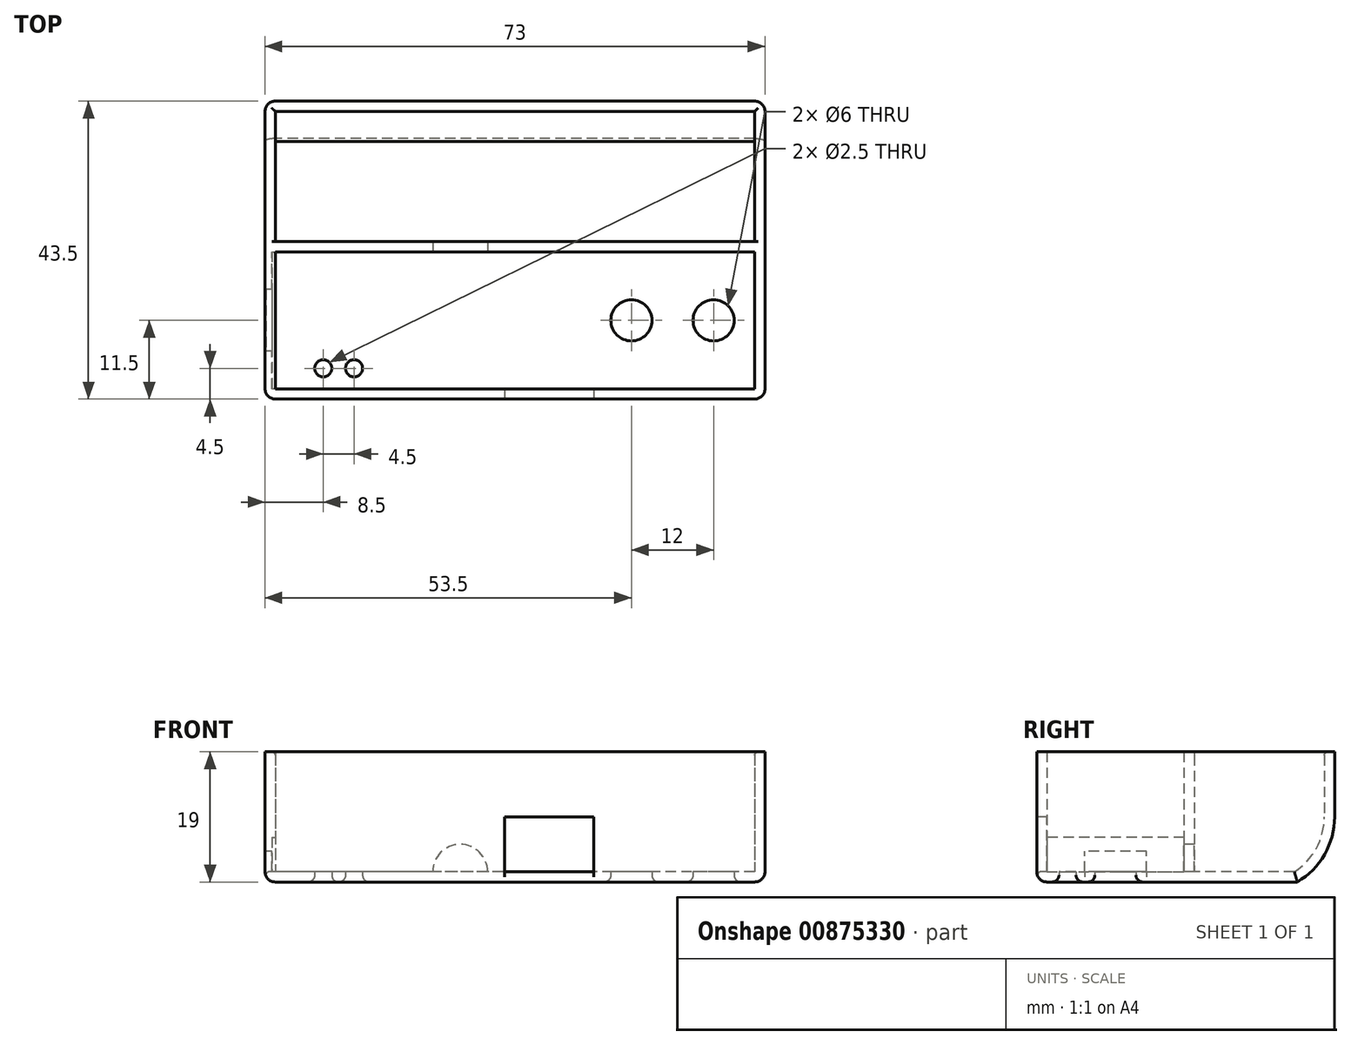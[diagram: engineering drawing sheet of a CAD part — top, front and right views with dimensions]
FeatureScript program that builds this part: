
annotation { "Feature Type Name" : "Feature", "Feature Type Description" : "" }
export const myFeature = defineFeature(function(context is Context, id is Id, definition is map)
    precondition{}
    {
        {
            var Q0;
            Q0=qCreatedBy(makeId("Top.planeOp"),FACE);
            var sketch = newSketch(context, id + "F0", { "sketchPlane" : qUnion([Q0])});
            skLineSegment(sketch, "E0.bottom", {"start": v(0, 0) * mm, "end": v(70, 0) * mm});
            skLineSegment(sketch, "E0.top", {"start": v(0, 19) * mm, "end": v(70, 19) * mm});
            skLineSegment(sketch, "E0.left", {"start": v(0, 0) * mm, "end": v(0, 19) * mm});
            skLineSegment(sketch, "E0.right", {"start": v(70, 0) * mm, "end": v(70, 19) * mm});
            skLineSegment(sketch, "E1.bottom", {"start": v(-1.5, 20.5) * mm, "end": v(71.5, 20.5) * mm});
            skLineSegment(sketch, "E1.top", {"start": v(-1.5, -1.5) * mm, "end": v(71.5, -1.5) * mm});
            skLineSegment(sketch, "E1.left", {"start": v(-1.5, 20.5) * mm, "end": v(-1.5, -1.5) * mm});
            skLineSegment(sketch, "E1.right", {"start": v(71.5, 20.5) * mm, "end": v(71.5, -1.5) * mm});
            skLineSegment(sketch, "E2.bottom", {"start": v(0, -1.5) * mm, "end": v(70, -1.5) * mm});
            skLineSegment(sketch, "E2.top", {"start": v(0, -21.5) * mm, "end": v(70, -21.5) * mm});
            skLineSegment(sketch, "E2.left", {"start": v(0, -1.5) * mm, "end": v(0, -21.5) * mm});
            skLineSegment(sketch, "E2.right", {"start": v(70, -1.5) * mm, "end": v(70, -21.5) * mm});
            skLineSegment(sketch, "E3.top", {"start": v(-1.5, -23) * mm, "end": v(71.5, -23) * mm});
            skLineSegment(sketch, "E3.left", {"start": v(-1.5, -1.5) * mm, "end": v(-1.5, -23) * mm});
            skLineSegment(sketch, "E3.right", {"start": v(71.5, -1.5) * mm, "end": v(71.5, -23) * mm});
            skCircle(sketch, "E4", {"center": v(64, -11.5) * mm, "radius": 3 * mm});
            skCircle(sketch, "E5", {"center": v(52, -11.5) * mm, "radius": 3 * mm});
            skLineSegment(sketch, "E6.bottom", {"start": v(70, -5) * mm, "end": v(46.5, -5) * mm, "construction": true});
            skLineSegment(sketch, "E6.top", {"start": v(70, -18) * mm, "end": v(46.5, -18) * mm, "construction": true});
            skLineSegment(sketch, "E6.left", {"start": v(70, -5) * mm, "end": v(70, -18) * mm, "construction": true});
            skLineSegment(sketch, "E6.right", {"start": v(46.5, -5) * mm, "end": v(46.5, -18) * mm, "construction": true});
            skLineSegment(sketch, "E7.top", {"start": v(46.5, -6) * mm, "end": v(33.5, -6) * mm, "construction": true});
            skLineSegment(sketch, "E7.right", {"start": v(33.5, -23) * mm, "end": v(33.5, -6) * mm, "construction": true});
            skLineSegment(sketch, "E8", {"start": v(33.5, -23) * mm, "end": v(46.5, -23) * mm});
            skLineSegment(sketch, "E9", {"start": v(46.5, -23) * mm, "end": v(46.5, -6) * mm, "construction": true});
            skLineSegment(sketch, "E10.bottom", {"start": v(0, -4) * mm, "end": v(33.5, -4) * mm, "construction": true});
            skLineSegment(sketch, "E10.top", {"start": v(0, -19) * mm, "end": v(33.5, -19) * mm, "construction": true});
            skLineSegment(sketch, "E10.left", {"start": v(0, -4) * mm, "end": v(0, -19) * mm, "construction": true});
            skLineSegment(sketch, "E10.right", {"start": v(33.5, -4) * mm, "end": v(33.5, -19) * mm, "construction": true});
            skLineSegment(sketch, "E11.bottom", {"start": v(0, -3) * mm, "end": v(27, -3) * mm, "construction": true});
            skLineSegment(sketch, "E11.top", {"start": v(0, -20) * mm, "end": v(27, -20) * mm, "construction": true});
            skLineSegment(sketch, "E11.left", {"start": v(0, -3) * mm, "end": v(0, -20) * mm, "construction": true});
            skLineSegment(sketch, "E11.right", {"start": v(27, -3) * mm, "end": v(27, -20) * mm, "construction": true});
            skLineSegment(sketch, "E12", {"start": v(40, -23) * mm, "end": v(40, -6) * mm, "construction": true});
            skLineSegment(sketch, "E13", {"start": v(0, -11.5) * mm, "end": v(27, -11.5) * mm, "construction": true});
            skCircle(sketch, "E14", {"center": v(7, -18.5) * mm, "radius": 1.25 * mm});
            skCircle(sketch, "E15", {"center": v(11.5, -18.5) * mm, "radius": 1.25 * mm});
            skSolve(sketch);
        }
        {
            var Q0;
            Q0=makeQuery(id+"F0.imprint","IMPRINT",FACE,{"disambiguationData":[TD([[makeQuery(id+"F0.imprint","IMPRINT",EDGE,{"derivedFrom":sQuery(id+"F0.wireOp",EDGE,"E0.bottom")}),1.0]])]});
            var Q1;
            Q1=makeQuery(id+"F0.imprint","IMPRINT",FACE,{"disambiguationData":[TD([[makeQuery(id+"F0.imprint","IMPRINT",EDGE,{"derivedFrom":sQuery(id+"F0.wireOp",EDGE,"E0.bottom")}),-1.0]])]});
            var Q2;
            Q2=makeQuery(id+"F0.imprint","IMPRINT",FACE,{"disambiguationData":[TD([[makeQuery(id+"F0.imprint","IMPRINT",EDGE,{"derivedFrom":sQuery(id+"F0.wireOp",EDGE,"E2.top")}),-1.0]])]});
            var Q3;
            Q3=makeQuery(id+"F0.imprint","IMPRINT",FACE,{"disambiguationData":[TD([[makeQuery(id+"F0.imprint","IMPRINT",EDGE,{"derivedFrom":sQuery(id+"F0.wireOp",EDGE,"E2.top")}),1.0]])]});
            extrude(context, id + "F1", {"entities" : qUnion([Q0, Q1, Q2, Q3]), "depth" : 1.5 * mm, "offsetDistance" : 25 * mm});
        }
        {
            var Q0;
            Q0=makeQuery(id+"F0.imprint","IMPRINT",FACE,{"disambiguationData":[TD([[makeQuery(id+"F0.imprint","IMPRINT",EDGE,{"derivedFrom":sQuery(id+"F0.wireOp",EDGE,"E0.bottom")}),-1.0]])]});
            var Q1;
            Q1=makeQuery(id+"F0.imprint","IMPRINT",FACE,{"disambiguationData":[TD([[makeQuery(id+"F0.imprint","IMPRINT",EDGE,{"derivedFrom":sQuery(id+"F0.wireOp",EDGE,"E2.top")}),-1.0]])]});
            extrude(context, id + "F2", {"entities" : qUnion([Q0, Q1]), "operationType" : NewBodyOperationType.ADD, "depth" : 19 * mm, "offsetDistance" : 25 * mm});
        }
        {
            var Q0;
            {var subQ0=sQuery(id+"F0.wireOp",EDGE,"E3.left");var subQ1=sQuery(id+"F0.wireOp",EDGE,"E1.left");Q0=makeQuery(id+"F2.boolean.opBoolean","MERGE",FACE,{"derivedFrom":[makeQuery(id+"F1.opExtrude","SWEPT_FACE",FACE,{"disambiguationData":[OSD([subQ1,subQ0])]}),makeQuery(id+"F2.opExtrude","SWEPT_FACE",FACE,{"disambiguationData":[OSD([subQ1,subQ0])]})]});}
            var sketch = newSketch(context, id + "F3", { "sketchPlane" : qUnion([Q0])});
            skCircle(sketch, "E16", {"center": v(-9.5, 9.5) * mm, "radius": 9.5 * mm});
            skCircle(sketch, "E17", {"center": v(-9.5, 9.5) * mm, "radius": 11 * mm});
            skLineSegment(sketch, "E18", {"start": v(-19, 19) * mm, "end": v(-19, 0) * mm, "construction": true});
            skLineSegment(sketch, "E19", {"start": v(-19, 3.95) * mm, "end": v(-19, 9.5) * mm});
            skSolve(sketch);
        }
        {
            var Q0;
            {var subQ0=sQuery(id+"F3.wireOp",EDGE,"E17");var subQ1=sQuery(id+"F0.wireOp",EDGE,"E1.left");var subQ5=makeQuery(id+"F1.opExtrude","CAP_EDGE",EDGE,{"disambiguationData":[OSD([subQ1,sQuery(id+"F0.wireOp",EDGE,"E3.left")])],"isStart":true});var subQ6=makeQuery(id+"F3.imprint","INTERSECT",VERTEX,{"disambiguationData":[OD(0.0)],"derivedFrom":[subQ5,subQ0]});Q0=makeQuery(id+"F3.imprint","IMPRINT",FACE,{"disambiguationData":[TD([[makeQuery(id+"F3.imprint","IMPRINT",EDGE,{"disambiguationData":[TD([[subQ6,1.0]])],"derivedFrom":subQ0}),-1.0]])]});}
            extrude(context, id + "F4", {"entities" : qUnion([Q0]), "operationType" : NewBodyOperationType.REMOVE, "endBound" : BoundingType.UP_TO_NEXT, "oppositeDirection" : true, "depth" : 25 * mm, "offsetDistance" : 25 * mm});
        }
        {
            var Q0;
            {var subQ0=sQuery(id+"F3.wireOp",EDGE,"E19");Q0=makeQuery(id+"F3.imprint","IMPRINT",FACE,{"disambiguationData":[TD([[makeQuery(id+"F3.imprint","IMPRINT",EDGE,{"derivedFrom":subQ0}),-1.0]])]});}
            extrude(context, id + "F5", {"entities" : qUnion([Q0]), "operationType" : NewBodyOperationType.ADD, "oppositeDirection" : true, "depth" : 72 * mm, "offsetDistance" : 25 * mm});
        }
        {
            var Q0;
            {var subQ0=sQuery(id+"F0.wireOp",EDGE,"E8");var subQ1=sQuery(id+"F0.wireOp",EDGE,"E3.top");Q0=makeQuery(id+"F2.boolean.opBoolean","MERGE",FACE,{"derivedFrom":[makeQuery(id+"F1.opExtrude","SWEPT_FACE",FACE,{"disambiguationData":[OSD([subQ1,subQ0])]}),makeQuery(id+"F2.opExtrude","SWEPT_FACE",FACE,{"disambiguationData":[OSD([subQ1,subQ0])]})]});}
            var sketch = newSketch(context, id + "F6", { "sketchPlane" : qUnion([Q0])});
            skLineSegment(sketch, "E20.bottom", {"start": v(33.5, 0) * mm, "end": v(46.5, 0) * mm});
            skLineSegment(sketch, "E20.top", {"start": v(33.5, 9.5) * mm, "end": v(46.5, 9.5) * mm});
            skLineSegment(sketch, "E20.left", {"start": v(33.5, 0) * mm, "end": v(33.5, 9.5) * mm});
            skLineSegment(sketch, "E20.right", {"start": v(46.5, 0) * mm, "end": v(46.5, 9.5) * mm});
            skLineSegment(sketch, "E21", {"start": v(46.5, 1.5) * mm, "end": v(33.5, 1.5) * mm});
            skSolve(sketch);
        }
        {
            var Q0;
            {var subQ0=sQuery(id+"F6.wireOp",EDGE,"E20.top");Q0=makeQuery(id+"F6.imprint","IMPRINT",FACE,{"disambiguationData":[TD([[makeQuery(id+"F6.imprint","IMPRINT",EDGE,{"derivedFrom":subQ0}),-1.0]])]});}
            extrude(context, id + "F7", {"entities" : qUnion([Q0]), "operationType" : NewBodyOperationType.REMOVE, "oppositeDirection" : true, "depth" : 1.5 * mm, "offsetDistance" : 25 * mm});
        }
        {
            var Q0;
            {var subQ0=sQuery(id+"F0.wireOp",EDGE,"E3.left");var subQ1=sQuery(id+"F0.wireOp",EDGE,"E1.left");Q0=makeQuery(id+"F2.boolean.opBoolean","MERGE",FACE,{"derivedFrom":[makeQuery(id+"F1.opExtrude","SWEPT_FACE",FACE,{"disambiguationData":[OSD([subQ1,subQ0])]}),makeQuery(id+"F2.opExtrude","SWEPT_FACE",FACE,{"disambiguationData":[OSD([subQ1,subQ0])]})]});}
            var sketch = newSketch(context, id + "F8", { "sketchPlane" : qUnion([Q0])});
            skLineSegment(sketch, "E22.bottom", {"start": v(7, 0) * mm, "end": v(16, 0) * mm});
            skLineSegment(sketch, "E22.top", {"start": v(7, 4.5) * mm, "end": v(16, 4.5) * mm});
            skLineSegment(sketch, "E22.left", {"start": v(7, 0) * mm, "end": v(7, 4.5) * mm});
            skLineSegment(sketch, "E22.right", {"start": v(16, 0) * mm, "end": v(16, 4.5) * mm});
            skLineSegment(sketch, "E23", {"start": v(7, 1.5) * mm, "end": v(16, 1.5) * mm});
            skSolve(sketch);
        }
        {
            var Q0;
            {var subQ0=sQuery(id+"F8.wireOp",EDGE,"E22.top");Q0=makeQuery(id+"F8.imprint","IMPRINT",FACE,{"disambiguationData":[TD([[makeQuery(id+"F8.imprint","IMPRINT",EDGE,{"derivedFrom":subQ0}),-1.0]])]});}
            extrude(context, id + "F9", {"entities" : qUnion([Q0]), "operationType" : NewBodyOperationType.REMOVE, "oppositeDirection" : true, "depth" : 1.5 * mm, "offsetDistance" : 25 * mm});
        }
        {
            var Q0;
            Q0=makeQuery(id+"F2.opExtrude","SWEPT_FACE",FACE,{"disambiguationData":[OSD([sQuery(id+"F0.wireOp",EDGE,"E2.left")])]});
            var sketch = newSketch(context, id + "F10", { "sketchPlane" : qUnion([Q0])});
            skLineSegment(sketch, "E24.bottom", {"start": v(-1.5, 1.5) * mm, "end": v(-21.5, 1.5) * mm});
            skLineSegment(sketch, "E24.top", {"start": v(-1.5, 6.5) * mm, "end": v(-21.5, 6.5) * mm});
            skLineSegment(sketch, "E24.left", {"start": v(-1.5, 1.5) * mm, "end": v(-1.5, 6.5) * mm});
            skLineSegment(sketch, "E24.right", {"start": v(-21.5, 1.5) * mm, "end": v(-21.5, 6.5) * mm});
            skSolve(sketch);
        }
        {
            var Q0;
            Q0=makeQuery(id+"F10.imprint","IMPRINT",FACE,{"disambiguationData":[TD([[makeQuery(id+"F10.imprint","IMPRINT",EDGE,{"derivedFrom":sQuery(id+"F10.wireOp",EDGE,"E24.top")}),1.0]])]});
            extrude(context, id + "F11", {"entities" : qUnion([Q0]), "operationType" : NewBodyOperationType.REMOVE, "oppositeDirection" : true, "depth" : 0.5 * mm, "offsetDistance" : 25 * mm});
        }
        {
            var Q0;
            Q0=makeQuery(id+"F11.boolean.opBoolean","MERGE",FACE,{"derivedFrom":[makeQuery(id+"F2.opExtrude","SWEPT_FACE",FACE,{"disambiguationData":[OSD([sQuery(id+"F0.wireOp",EDGE,"E1.top")])]})],"fromTools":[makeQuery(id+"F11.opExtrude","SWEPT_FACE",FACE,{"disambiguationData":[OSD([sQuery(id+"F10.wireOp",EDGE,"E24.left")])]})]});
            var sketch = newSketch(context, id + "F12", { "sketchPlane" : qUnion([Q0])});
            skCircle(sketch, "E25", {"center": v(27, 1.5) * mm, "radius": 4 * mm});
            skSolve(sketch);
        }
        {
            var Q0;
            {var subQ0=sQuery(id+"F12.wireOp",EDGE,"E25");var subQ1=makeQuery(id+"F11.boolean.opBoolean","MERGE",EDGE,{"derivedFrom":[makeQuery(id+"F2.boolean.opBoolean","INTERSECT",EDGE,{"derivedFrom":[makeQuery(id+"F1.opExtrude","CAP_FACE",FACE,{"disambiguationData":[OSD([sQuery(id+"F0.wireOp",EDGE,"E1.bottom"),sQuery(id+"F0.wireOp",EDGE,"E1.left"),sQuery(id+"F0.wireOp",EDGE,"E1.right"),sQuery(id+"F0.wireOp",EDGE,"E3.top"),sQuery(id+"F0.wireOp",EDGE,"E3.left"),sQuery(id+"F0.wireOp",EDGE,"E3.right"),sQuery(id+"F0.wireOp",EDGE,"E4"),sQuery(id+"F0.wireOp",EDGE,"E5"),sQuery(id+"F0.wireOp",EDGE,"E8"),sQuery(id+"F0.wireOp",EDGE,"E14"),sQuery(id+"F0.wireOp",EDGE,"E15")])],"isStart":false}),makeQuery(id+"F2.opExtrude","SWEPT_FACE",FACE,{"disambiguationData":[OSD([sQuery(id+"F0.wireOp",EDGE,"E1.top")])]})]})],"fromTools":[makeQuery(id+"F11.opExtrude","SWEPT_EDGE",EDGE,{"disambiguationData":[OSD([sQuery(id+"F10.wireOp",EDGE,"E24.bottom"),sQuery(id+"F10.wireOp",EDGE,"E24.left")])]})]});var subQ2=makeQuery(id+"F12.imprint","INTERSECT",VERTEX,{"disambiguationData":[OD(0.0)],"derivedFrom":[subQ1,subQ0]});Q0=makeQuery(id+"F12.imprint","IMPRINT",FACE,{"disambiguationData":[TD([[makeQuery(id+"F12.imprint","IMPRINT",EDGE,{"disambiguationData":[TD([[subQ2,-1.0]])],"derivedFrom":subQ0}),1.0]])]});}
            extrude(context, id + "F13", {"entities" : qUnion([Q0]), "operationType" : NewBodyOperationType.REMOVE, "oppositeDirection" : true, "depth" : 1.5 * mm, "offsetDistance" : 25 * mm});
        }
        {
            var Q0;
            {var subQ0=sQuery(id+"F0.wireOp",EDGE,"E3.left");var subQ1=sQuery(id+"F0.wireOp",EDGE,"E3.top");Q0=makeQuery(id+"F2.boolean.opBoolean","MERGE",EDGE,{"derivedFrom":[makeQuery(id+"F1.opExtrude","SWEPT_EDGE",EDGE,{"disambiguationData":[OSD([subQ1,subQ0])]}),makeQuery(id+"F2.opExtrude","SWEPT_EDGE",EDGE,{"disambiguationData":[OSD([subQ1,subQ0])]})]});}
            var Q1;
            Q1=makeQuery(id+"F1.opExtrude","CAP_EDGE",EDGE,{"disambiguationData":[OSD([sQuery(id+"F0.wireOp",EDGE,"E1.left"),sQuery(id+"F0.wireOp",EDGE,"E3.left")])],"isStart":true});
            var Q2;
            Q2=makeQuery(id+"F1.opExtrude","CAP_EDGE",EDGE,{"disambiguationData":[OSD([sQuery(id+"F0.wireOp",EDGE,"E3.top"),sQuery(id+"F0.wireOp",EDGE,"E8")])],"isStart":true});
            var Q3;
            {var subQ0=sQuery(id+"F0.wireOp",EDGE,"E3.right");var subQ1=sQuery(id+"F0.wireOp",EDGE,"E3.top");Q3=makeQuery(id+"F2.boolean.opBoolean","MERGE",EDGE,{"derivedFrom":[makeQuery(id+"F1.opExtrude","SWEPT_EDGE",EDGE,{"disambiguationData":[OSD([subQ1,subQ0])]}),makeQuery(id+"F2.opExtrude","SWEPT_EDGE",EDGE,{"disambiguationData":[OSD([subQ1,subQ0])]})]});}
            var Q4;
            {var subQ0=sQuery(id+"F0.wireOp",EDGE,"E1.right");var subQ1=sQuery(id+"F0.wireOp",EDGE,"E1.bottom");Q4=makeQuery(id+"F2.boolean.opBoolean","MERGE",EDGE,{"derivedFrom":[makeQuery(id+"F1.opExtrude","SWEPT_EDGE",EDGE,{"disambiguationData":[OSD([subQ1,subQ0])]}),makeQuery(id+"F2.opExtrude","SWEPT_EDGE",EDGE,{"disambiguationData":[OSD([subQ1,subQ0])]})]});}
            var Q5;
            Q5=makeQuery(id+"F4.boolean.opBoolean","COPY",EDGE,{"derivedFrom":makeQuery(id+"F4.opExtrude","CAP_EDGE",EDGE,{"disambiguationData":[OSD([sQuery(id+"F3.wireOp",EDGE,"E17")])],"isStart":false})});
            var Q6;
            Q6=makeQuery(id+"F1.opExtrude","CAP_EDGE",EDGE,{"disambiguationData":[OSD([sQuery(id+"F0.wireOp",EDGE,"E1.right"),sQuery(id+"F0.wireOp",EDGE,"E3.right")])],"isStart":true});
            var Q7;
            {var subQ0=sQuery(id+"F0.wireOp",EDGE,"E1.left");var subQ1=sQuery(id+"F0.wireOp",EDGE,"E1.bottom");Q7=makeQuery(id+"F2.boolean.opBoolean","MERGE",EDGE,{"derivedFrom":[makeQuery(id+"F1.opExtrude","SWEPT_EDGE",EDGE,{"disambiguationData":[OSD([subQ1,subQ0])]}),makeQuery(id+"F2.opExtrude","SWEPT_EDGE",EDGE,{"disambiguationData":[OSD([subQ1,subQ0])]})]});}
            var Q8;
            Q8=makeQuery(id+"F4.boolean.opBoolean","COPY",EDGE,{"derivedFrom":makeQuery(id+"F4.opExtrude","CAP_EDGE",EDGE,{"disambiguationData":[OSD([sQuery(id+"F3.wireOp",EDGE,"E17")])],"isStart":true})});
            fillet(context, id + "F14", {"entities" : qUnion([Q0, Q1, Q2, Q3, Q4, Q5, Q6, Q7, Q8]), "radius" : 1.5 * mm, "tangentPropagation" : true, "allowEdgeOverflow" : false});
        }
        {
            var Q0;
            Q0=makeQuery(id+"F1.opExtrude","CAP_EDGE",EDGE,{"disambiguationData":[OSD([sQuery(id+"F0.wireOp",EDGE,"E5")])],"isStart":true});
            var Q1;
            Q1=makeQuery(id+"F1.opExtrude","CAP_EDGE",EDGE,{"disambiguationData":[OSD([sQuery(id+"F0.wireOp",EDGE,"E4")])],"isStart":true});
            var Q2;
            Q2=makeQuery(id+"F1.opExtrude","CAP_EDGE",EDGE,{"disambiguationData":[OSD([sQuery(id+"F0.wireOp",EDGE,"E14")])],"isStart":true});
            var Q3;
            Q3=makeQuery(id+"F1.opExtrude","CAP_EDGE",EDGE,{"disambiguationData":[OSD([sQuery(id+"F0.wireOp",EDGE,"E15")])],"isStart":true});
            var Q4;
            Q4=makeQuery(id+"F9.boolean.opBoolean","COPY",EDGE,{"derivedFrom":makeQuery(id+"F9.opExtrude","CAP_EDGE",EDGE,{"disambiguationData":[OSD([sQuery(id+"F8.wireOp",EDGE,"E22.top")])],"isStart":true})});
            var Q5;
            Q5=makeQuery(id+"F9.boolean.opBoolean","COPY",EDGE,{"derivedFrom":makeQuery(id+"F9.opExtrude","CAP_EDGE",EDGE,{"disambiguationData":[OSD([sQuery(id+"F8.wireOp",EDGE,"E22.right")])],"isStart":true})});
            var Q6;
            Q6=makeQuery(id+"F9.boolean.opBoolean","COPY",EDGE,{"derivedFrom":makeQuery(id+"F9.opExtrude","CAP_EDGE",EDGE,{"disambiguationData":[OSD([sQuery(id+"F8.wireOp",EDGE,"E22.left")])],"isStart":true})});
            var Q7;
            Q7=makeQuery(id+"F7.boolean.opBoolean","COPY",EDGE,{"derivedFrom":makeQuery(id+"F7.opExtrude","CAP_EDGE",EDGE,{"disambiguationData":[OSD([sQuery(id+"F6.wireOp",EDGE,"E20.top")])],"isStart":true})});
            var Q8;
            Q8=makeQuery(id+"F7.boolean.opBoolean","COPY",EDGE,{"derivedFrom":makeQuery(id+"F7.opExtrude","CAP_EDGE",EDGE,{"disambiguationData":[OSD([sQuery(id+"F6.wireOp",EDGE,"E20.right")])],"isStart":true})});
            var Q9;
            Q9=makeQuery(id+"F7.boolean.opBoolean","COPY",EDGE,{"derivedFrom":makeQuery(id+"F7.opExtrude","CAP_EDGE",EDGE,{"disambiguationData":[OSD([sQuery(id+"F6.wireOp",EDGE,"E20.left")])],"isStart":true})});
            var Q10;
            Q10=makeQuery(id+"F13.boolean.opBoolean","COPY",EDGE,{"derivedFrom":makeQuery(id+"F13.opExtrude","CAP_EDGE",EDGE,{"disambiguationData":[OSD([sQuery(id+"F12.wireOp",EDGE,"E25")])],"isStart":true})});
            var Q11;
            Q11=makeQuery(id+"F13.boolean.opBoolean","COPY",EDGE,{"derivedFrom":makeQuery(id+"F13.opExtrude","CAP_EDGE",EDGE,{"disambiguationData":[OSD([sQuery(id+"F12.wireOp",EDGE,"E25")])],"isStart":false})});
            fillet(context, id + "F15", {"entities" : qUnion([Q0, Q1, Q2, Q3, Q4, Q5, Q6, Q7, Q8, Q9, Q10, Q11]), "radius" : 1 * mm, "tangentPropagation" : true, "allowEdgeOverflow" : false});
        }
        {
            var Q0;
            {var subQ0=sQuery(id+"F0.wireOp",EDGE,"E8");var subQ1=sQuery(id+"F0.wireOp",EDGE,"E3.top");var subQ2=makeQuery(id+"F2.boolean.opBoolean","MERGE",FACE,{"derivedFrom":[makeQuery(id+"F1.opExtrude","SWEPT_FACE",FACE,{"disambiguationData":[OSD([subQ1,subQ0])]}),makeQuery(id+"F2.opExtrude","SWEPT_FACE",FACE,{"disambiguationData":[OSD([subQ1,subQ0])]})]});var subQ3=makeQuery(id+"F1.opExtrude","CAP_EDGE",EDGE,{"disambiguationData":[OSD([subQ1,subQ0])],"isStart":true});var subQ4=sQuery(id+"F10.wireOp",EDGE,"E24.left");var subQ5=sQuery(id+"F10.wireOp",EDGE,"E24.bottom");var subQ6=sQuery(id+"F0.wireOp",EDGE,"E15");var subQ7=sQuery(id+"F0.wireOp",EDGE,"E14");var subQ8=sQuery(id+"F0.wireOp",EDGE,"E5");var subQ9=sQuery(id+"F0.wireOp",EDGE,"E4");var subQ10=sQuery(id+"F0.wireOp",EDGE,"E3.right");var subQ11=sQuery(id+"F0.wireOp",EDGE,"E3.left");var subQ12=sQuery(id+"F0.wireOp",EDGE,"E1.top");var subQ13=sQuery(id+"F0.wireOp",EDGE,"E1.right");var subQ14=sQuery(id+"F0.wireOp",EDGE,"E1.left");var subQ15=sQuery(id+"F0.wireOp",EDGE,"E1.bottom");var subQ16=makeQuery(id+"F1.opExtrude","CAP_FACE",FACE,{"disambiguationData":[OSD([subQ15,subQ14,subQ13,subQ1,subQ11,subQ10,subQ9,subQ8,subQ0,subQ7,subQ6])],"isStart":false});Q0=makeQuery(id+"F15.opFillet","MERGE",EDGE,{"derivedFrom":[makeQuery(id+"F14.opFillet","BLEND_EDGE",EDGE,{"blendedFrom":[subQ3,makeQuery(id+"F13.boolean.opBoolean","MERGE",FACE,{"derivedFrom":[makeQuery(id+"F2.boolean.opBoolean","SPLIT",FACE,{"disambiguationData":[TD([makeQuery(id+"F2.opExtrude","SWEPT_FACE",FACE,{"disambiguationData":[OSD([sQuery(id+"F0.wireOp",EDGE,"E0.bottom")])]})])],"derivedFrom":subQ16}),makeQuery(id+"F11.boolean.opBoolean","MERGE",FACE,{"derivedFrom":[makeQuery(id+"F9.boolean.opBoolean","MERGE",FACE,{"derivedFrom":[makeQuery(id+"F7.boolean.opBoolean","MERGE",FACE,{"derivedFrom":[makeQuery(id+"F2.boolean.opBoolean","SPLIT",FACE,{"disambiguationData":[TD([makeQuery(id+"F1.opExtrude","SWEPT_FACE",FACE,{"disambiguationData":[OSD([subQ9])]})])],"derivedFrom":subQ16})],"fromTools":[makeQuery(id+"F7.opExtrude","SWEPT_FACE",FACE,{"disambiguationData":[OSD([sQuery(id+"F6.wireOp",EDGE,"E21")])]})]})],"fromTools":[makeQuery(id+"F9.opExtrude","SWEPT_FACE",FACE,{"disambiguationData":[OSD([sQuery(id+"F8.wireOp",EDGE,"E23")])]})]})],"fromTools":[makeQuery(id+"F11.opExtrude","SWEPT_FACE",FACE,{"disambiguationData":[OSD([subQ5]),TDD([makeQuery(id+"F10.imprint","IMPRINT",EDGE,{"disambiguationData":[TD([[makeQuery(id+"F10.imprint","INTERSECT",VERTEX,{"derivedFrom":[subQ5,sQuery(id+"F10.wireOp",EDGE,"E24.right")]}),-1.0],[makeQuery(id+"F10.imprint","INTERSECT",VERTEX,{"derivedFrom":[makeQuery(id+"F9.boolean.opBoolean","COPY",EDGE,{"derivedFrom":makeQuery(id+"F9.opExtrude","CAP_EDGE",EDGE,{"disambiguationData":[OSD([sQuery(id+"F8.wireOp",EDGE,"E22.right")])],"isStart":false})}),subQ5]}),1.0]])],"derivedFrom":subQ5})])]}),makeQuery(id+"F11.opExtrude","SWEPT_FACE",FACE,{"disambiguationData":[OSD([subQ5]),TDD([makeQuery(id+"F10.imprint","IMPRINT",EDGE,{"disambiguationData":[TD([[makeQuery(id+"F10.imprint","INTERSECT",VERTEX,{"derivedFrom":[subQ5,subQ4]}),1.0],[makeQuery(id+"F10.imprint","INTERSECT",VERTEX,{"derivedFrom":[makeQuery(id+"F9.boolean.opBoolean","COPY",EDGE,{"derivedFrom":makeQuery(id+"F9.opExtrude","CAP_EDGE",EDGE,{"disambiguationData":[OSD([sQuery(id+"F8.wireOp",EDGE,"E22.left")])],"isStart":false})}),subQ5]}),-1.0]])],"derivedFrom":subQ5})])]})]})],"fromTools":[makeQuery(id+"F13.opExtrude","SWEPT_FACE",FACE,{"disambiguationData":[OSD([subQ15,subQ14,subQ13,subQ12,subQ1,subQ11,subQ10,subQ9,subQ8,subQ0,subQ7,subQ6,subQ5,subQ4])]})]})],"blendedInto":[makeQuery(id+"F13.boolean.opBoolean","MERGE",FACE,{"derivedFrom":[makeQuery(id+"F2.boolean.opBoolean","SPLIT",FACE,{"disambiguationData":[TD([makeQuery(id+"F2.opExtrude","SWEPT_FACE",FACE,{"disambiguationData":[OSD([sQuery(id+"F0.wireOp",EDGE,"E0.bottom")])]})])],"derivedFrom":subQ16}),makeQuery(id+"F11.boolean.opBoolean","MERGE",FACE,{"derivedFrom":[makeQuery(id+"F9.boolean.opBoolean","MERGE",FACE,{"derivedFrom":[makeQuery(id+"F7.boolean.opBoolean","MERGE",FACE,{"derivedFrom":[makeQuery(id+"F2.boolean.opBoolean","SPLIT",FACE,{"disambiguationData":[TD([makeQuery(id+"F1.opExtrude","SWEPT_FACE",FACE,{"disambiguationData":[OSD([subQ9])]})])],"derivedFrom":subQ16})],"fromTools":[makeQuery(id+"F7.opExtrude","SWEPT_FACE",FACE,{"disambiguationData":[OSD([sQuery(id+"F6.wireOp",EDGE,"E21")])]})]})],"fromTools":[makeQuery(id+"F9.opExtrude","SWEPT_FACE",FACE,{"disambiguationData":[OSD([sQuery(id+"F8.wireOp",EDGE,"E23")])]})]})],"fromTools":[makeQuery(id+"F11.opExtrude","SWEPT_FACE",FACE,{"disambiguationData":[OSD([subQ5]),TDD([makeQuery(id+"F10.imprint","IMPRINT",EDGE,{"disambiguationData":[TD([[makeQuery(id+"F10.imprint","INTERSECT",VERTEX,{"derivedFrom":[subQ5,sQuery(id+"F10.wireOp",EDGE,"E24.right")]}),-1.0],[makeQuery(id+"F10.imprint","INTERSECT",VERTEX,{"derivedFrom":[makeQuery(id+"F9.boolean.opBoolean","COPY",EDGE,{"derivedFrom":makeQuery(id+"F9.opExtrude","CAP_EDGE",EDGE,{"disambiguationData":[OSD([sQuery(id+"F8.wireOp",EDGE,"E22.right")])],"isStart":false})}),subQ5]}),1.0]])],"derivedFrom":subQ5})])]}),makeQuery(id+"F11.opExtrude","SWEPT_FACE",FACE,{"disambiguationData":[OSD([subQ5]),TDD([makeQuery(id+"F10.imprint","IMPRINT",EDGE,{"disambiguationData":[TD([[makeQuery(id+"F10.imprint","INTERSECT",VERTEX,{"derivedFrom":[subQ5,subQ4]}),1.0],[makeQuery(id+"F10.imprint","INTERSECT",VERTEX,{"derivedFrom":[makeQuery(id+"F9.boolean.opBoolean","COPY",EDGE,{"derivedFrom":makeQuery(id+"F9.opExtrude","CAP_EDGE",EDGE,{"disambiguationData":[OSD([sQuery(id+"F8.wireOp",EDGE,"E22.left")])],"isStart":false})}),subQ5]}),-1.0]])],"derivedFrom":subQ5})])]})]})],"fromTools":[makeQuery(id+"F13.opExtrude","SWEPT_FACE",FACE,{"disambiguationData":[OSD([subQ15,subQ14,subQ13,subQ12,subQ1,subQ11,subQ10,subQ9,subQ8,subQ0,subQ7,subQ6,subQ5,subQ4])]})]})]}),makeQuery(id+"F14.opFillet","BLEND_EDGE",EDGE,{"disambiguationData":[OD(0.0)],"blendedFrom":[subQ3,subQ2],"blendedInto":[subQ2]}),makeQuery(id+"F14.opFillet","BLEND_EDGE",EDGE,{"disambiguationData":[OD(1.0)],"blendedFrom":[subQ3,subQ2],"blendedInto":[subQ2]})]});}
            var Q1;
            {var subQ0=sQuery(id+"F0.wireOp",EDGE,"E3.left");var subQ1=sQuery(id+"F0.wireOp",EDGE,"E1.left");var subQ2=makeQuery(id+"F2.boolean.opBoolean","MERGE",FACE,{"derivedFrom":[makeQuery(id+"F1.opExtrude","SWEPT_FACE",FACE,{"disambiguationData":[OSD([subQ1,subQ0])]}),makeQuery(id+"F2.opExtrude","SWEPT_FACE",FACE,{"disambiguationData":[OSD([subQ1,subQ0])]})]});var subQ3=makeQuery(id+"F1.opExtrude","CAP_EDGE",EDGE,{"disambiguationData":[OSD([subQ1,subQ0])],"isStart":true});var subQ4=sQuery(id+"F10.wireOp",EDGE,"E24.left");var subQ5=sQuery(id+"F10.wireOp",EDGE,"E24.bottom");var subQ6=sQuery(id+"F0.wireOp",EDGE,"E15");var subQ7=sQuery(id+"F0.wireOp",EDGE,"E14");var subQ8=sQuery(id+"F0.wireOp",EDGE,"E8");var subQ9=sQuery(id+"F0.wireOp",EDGE,"E5");var subQ10=sQuery(id+"F0.wireOp",EDGE,"E4");var subQ11=sQuery(id+"F0.wireOp",EDGE,"E3.right");var subQ12=sQuery(id+"F0.wireOp",EDGE,"E3.top");var subQ13=sQuery(id+"F0.wireOp",EDGE,"E1.top");var subQ14=sQuery(id+"F0.wireOp",EDGE,"E1.right");var subQ15=sQuery(id+"F0.wireOp",EDGE,"E1.bottom");var subQ16=makeQuery(id+"F1.opExtrude","CAP_FACE",FACE,{"disambiguationData":[OSD([subQ15,subQ1,subQ14,subQ12,subQ0,subQ11,subQ10,subQ9,subQ8,subQ7,subQ6])],"isStart":false});Q1=makeQuery(id+"F15.opFillet","MERGE",EDGE,{"derivedFrom":[makeQuery(id+"F14.opFillet","BLEND_EDGE",EDGE,{"blendedFrom":[subQ3,makeQuery(id+"F13.boolean.opBoolean","MERGE",FACE,{"derivedFrom":[makeQuery(id+"F2.boolean.opBoolean","SPLIT",FACE,{"disambiguationData":[TD([makeQuery(id+"F2.opExtrude","SWEPT_FACE",FACE,{"disambiguationData":[OSD([sQuery(id+"F0.wireOp",EDGE,"E0.bottom")])]})])],"derivedFrom":subQ16}),makeQuery(id+"F11.boolean.opBoolean","MERGE",FACE,{"derivedFrom":[makeQuery(id+"F9.boolean.opBoolean","MERGE",FACE,{"derivedFrom":[makeQuery(id+"F7.boolean.opBoolean","MERGE",FACE,{"derivedFrom":[makeQuery(id+"F2.boolean.opBoolean","SPLIT",FACE,{"disambiguationData":[TD([makeQuery(id+"F1.opExtrude","SWEPT_FACE",FACE,{"disambiguationData":[OSD([subQ10])]})])],"derivedFrom":subQ16})],"fromTools":[makeQuery(id+"F7.opExtrude","SWEPT_FACE",FACE,{"disambiguationData":[OSD([sQuery(id+"F6.wireOp",EDGE,"E21")])]})]})],"fromTools":[makeQuery(id+"F9.opExtrude","SWEPT_FACE",FACE,{"disambiguationData":[OSD([sQuery(id+"F8.wireOp",EDGE,"E23")])]})]})],"fromTools":[makeQuery(id+"F11.opExtrude","SWEPT_FACE",FACE,{"disambiguationData":[OSD([subQ5]),TDD([makeQuery(id+"F10.imprint","IMPRINT",EDGE,{"disambiguationData":[TD([[makeQuery(id+"F10.imprint","INTERSECT",VERTEX,{"derivedFrom":[subQ5,sQuery(id+"F10.wireOp",EDGE,"E24.right")]}),-1.0],[makeQuery(id+"F10.imprint","INTERSECT",VERTEX,{"derivedFrom":[makeQuery(id+"F9.boolean.opBoolean","COPY",EDGE,{"derivedFrom":makeQuery(id+"F9.opExtrude","CAP_EDGE",EDGE,{"disambiguationData":[OSD([sQuery(id+"F8.wireOp",EDGE,"E22.right")])],"isStart":false})}),subQ5]}),1.0]])],"derivedFrom":subQ5})])]}),makeQuery(id+"F11.opExtrude","SWEPT_FACE",FACE,{"disambiguationData":[OSD([subQ5]),TDD([makeQuery(id+"F10.imprint","IMPRINT",EDGE,{"disambiguationData":[TD([[makeQuery(id+"F10.imprint","INTERSECT",VERTEX,{"derivedFrom":[subQ5,subQ4]}),1.0],[makeQuery(id+"F10.imprint","INTERSECT",VERTEX,{"derivedFrom":[makeQuery(id+"F9.boolean.opBoolean","COPY",EDGE,{"derivedFrom":makeQuery(id+"F9.opExtrude","CAP_EDGE",EDGE,{"disambiguationData":[OSD([sQuery(id+"F8.wireOp",EDGE,"E22.left")])],"isStart":false})}),subQ5]}),-1.0]])],"derivedFrom":subQ5})])]})]})],"fromTools":[makeQuery(id+"F13.opExtrude","SWEPT_FACE",FACE,{"disambiguationData":[OSD([subQ15,subQ1,subQ14,subQ13,subQ12,subQ0,subQ11,subQ10,subQ9,subQ8,subQ7,subQ6,subQ5,subQ4])]})]})],"blendedInto":[makeQuery(id+"F13.boolean.opBoolean","MERGE",FACE,{"derivedFrom":[makeQuery(id+"F2.boolean.opBoolean","SPLIT",FACE,{"disambiguationData":[TD([makeQuery(id+"F2.opExtrude","SWEPT_FACE",FACE,{"disambiguationData":[OSD([sQuery(id+"F0.wireOp",EDGE,"E0.bottom")])]})])],"derivedFrom":subQ16}),makeQuery(id+"F11.boolean.opBoolean","MERGE",FACE,{"derivedFrom":[makeQuery(id+"F9.boolean.opBoolean","MERGE",FACE,{"derivedFrom":[makeQuery(id+"F7.boolean.opBoolean","MERGE",FACE,{"derivedFrom":[makeQuery(id+"F2.boolean.opBoolean","SPLIT",FACE,{"disambiguationData":[TD([makeQuery(id+"F1.opExtrude","SWEPT_FACE",FACE,{"disambiguationData":[OSD([subQ10])]})])],"derivedFrom":subQ16})],"fromTools":[makeQuery(id+"F7.opExtrude","SWEPT_FACE",FACE,{"disambiguationData":[OSD([sQuery(id+"F6.wireOp",EDGE,"E21")])]})]})],"fromTools":[makeQuery(id+"F9.opExtrude","SWEPT_FACE",FACE,{"disambiguationData":[OSD([sQuery(id+"F8.wireOp",EDGE,"E23")])]})]})],"fromTools":[makeQuery(id+"F11.opExtrude","SWEPT_FACE",FACE,{"disambiguationData":[OSD([subQ5]),TDD([makeQuery(id+"F10.imprint","IMPRINT",EDGE,{"disambiguationData":[TD([[makeQuery(id+"F10.imprint","INTERSECT",VERTEX,{"derivedFrom":[subQ5,sQuery(id+"F10.wireOp",EDGE,"E24.right")]}),-1.0],[makeQuery(id+"F10.imprint","INTERSECT",VERTEX,{"derivedFrom":[makeQuery(id+"F9.boolean.opBoolean","COPY",EDGE,{"derivedFrom":makeQuery(id+"F9.opExtrude","CAP_EDGE",EDGE,{"disambiguationData":[OSD([sQuery(id+"F8.wireOp",EDGE,"E22.right")])],"isStart":false})}),subQ5]}),1.0]])],"derivedFrom":subQ5})])]}),makeQuery(id+"F11.opExtrude","SWEPT_FACE",FACE,{"disambiguationData":[OSD([subQ5]),TDD([makeQuery(id+"F10.imprint","IMPRINT",EDGE,{"disambiguationData":[TD([[makeQuery(id+"F10.imprint","INTERSECT",VERTEX,{"derivedFrom":[subQ5,subQ4]}),1.0],[makeQuery(id+"F10.imprint","INTERSECT",VERTEX,{"derivedFrom":[makeQuery(id+"F9.boolean.opBoolean","COPY",EDGE,{"derivedFrom":makeQuery(id+"F9.opExtrude","CAP_EDGE",EDGE,{"disambiguationData":[OSD([sQuery(id+"F8.wireOp",EDGE,"E22.left")])],"isStart":false})}),subQ5]}),-1.0]])],"derivedFrom":subQ5})])]})]})],"fromTools":[makeQuery(id+"F13.opExtrude","SWEPT_FACE",FACE,{"disambiguationData":[OSD([subQ15,subQ1,subQ14,subQ13,subQ12,subQ0,subQ11,subQ10,subQ9,subQ8,subQ7,subQ6,subQ5,subQ4])]})]})]}),makeQuery(id+"F14.opFillet","BLEND_EDGE",EDGE,{"disambiguationData":[OD(0.0)],"blendedFrom":[subQ3,subQ2],"blendedInto":[subQ2]}),makeQuery(id+"F14.opFillet","BLEND_EDGE",EDGE,{"disambiguationData":[OD(1.0)],"blendedFrom":[subQ3,subQ2],"blendedInto":[subQ2]})]});}
            var Q2;
            Q2=makeQuery(id+"F2.opExtrude","CAP_EDGE",EDGE,{"disambiguationData":[OSD([sQuery(id+"F0.wireOp",EDGE,"E0.top")])],"isStart":false});
            var Q3;
            Q3=makeQuery(id+"F2.opExtrude","CAP_EDGE",EDGE,{"disambiguationData":[OSD([sQuery(id+"F0.wireOp",EDGE,"E0.right")])],"isStart":false});
            var Q4;
            Q4=makeQuery(id+"F2.opExtrude","CAP_EDGE",EDGE,{"disambiguationData":[OSD([sQuery(id+"F0.wireOp",EDGE,"E0.left")])],"isStart":false});
            fillet(context, id + "F16", {"entities" : qUnion([Q0, Q1, Q2, Q3, Q4]), "radius" : 0.5 * mm, "tangentPropagation" : true, "allowEdgeOverflow" : false});
        }
    });
